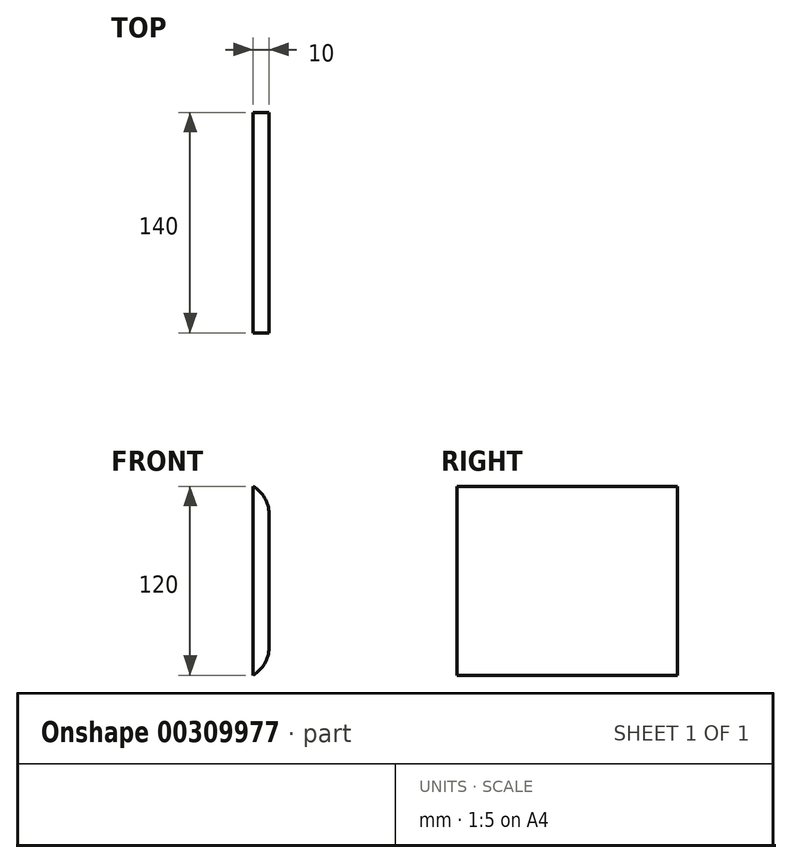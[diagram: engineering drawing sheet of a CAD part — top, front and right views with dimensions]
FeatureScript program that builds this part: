
annotation { "Feature Type Name" : "Feature", "Feature Type Description" : "" }
export const myFeature = defineFeature(function(context is Context, id is Id, definition is map)
    precondition{}
    {
        {
            var Q0;
            Q0=qCreatedBy(makeId("Front.planeOp"),FACE);
            var sketch = newSketch(context, id + "F0", { "sketchPlane" : qUnion([Q0])});
            skLineSegment(sketch, "E0.bottom", {"start": v(-5, 60) * mm, "end": v(5, 60) * mm});
            skLineSegment(sketch, "E0.top", {"start": v(-5, -60) * mm, "end": v(5, -60) * mm});
            skLineSegment(sketch, "E0.left", {"start": v(-5, 60) * mm, "end": v(-5, -60) * mm});
            skLineSegment(sketch, "E0.right", {"start": v(5, 60) * mm, "end": v(5, -60) * mm});
            skPoint(sketch, "E0.middle", {"position": v(0, 0) * mm});
            skSolve(sketch);
        }
        {
            var Q0;
            Q0 = qSketchRegion(id + "F0", true);
            extrude(context, id + "F1", {"entities" : qUnion([Q0]), "depth" : 140 * mm});
        }
        {
            var Q0;
            Q0=makeQuery(id+"F1.opExtrude","SWEPT_EDGE",EDGE,{"disambiguationData":[OSD([sQuery(id+"F0.wireOp",EDGE,"E0.bottom"),sQuery(id+"F0.wireOp",EDGE,"E0.right")])]});
            var Q1;
            Q1=makeQuery(id+"F1.opExtrude","SWEPT_EDGE",EDGE,{"disambiguationData":[OSD([sQuery(id+"F0.wireOp",EDGE,"E0.top"),sQuery(id+"F0.wireOp",EDGE,"E0.right")])]});
            fillet(context, id + "F2", {"entities" : qUnion([Q0, Q1]), "radius" : 20 * mm, "tangentPropagation" : true, "allowEdgeOverflow" : false});
        }
    });
